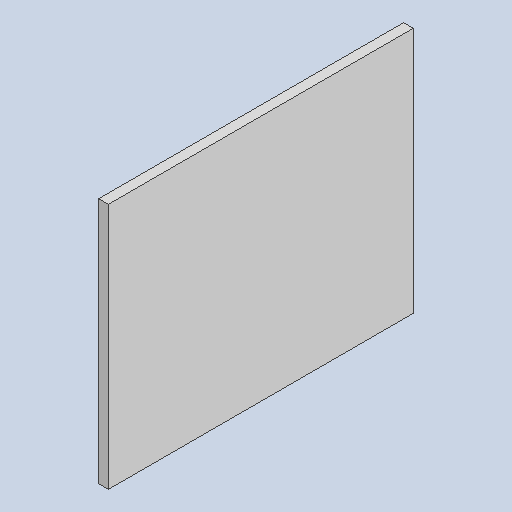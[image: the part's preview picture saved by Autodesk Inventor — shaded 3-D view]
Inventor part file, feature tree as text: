
AUTODESK INVENTOR PART (.ipt)
format: ipt  version: 2023 (Build 270158030, 158C)  size: 166,400 bytes
history: native  units: mm
features: extrude x4, sketch x4, other x3, reference x2
ambient origin geometry x8: Origin, YZ Plane, XZ Plane, XY Plane, X Axis, Y Axis, Z Axis, Center Point
bodies: Solid1 (feature_tree)
feature tree (13):
  extrude  "Extrusion1"  Depth=5.6mm
  extrude  "Extrusion2"  Depth=14.0mm
  extrude  "Extrusion3"  Depth=489.0mm
  extrude  "Extrusion4"  Depth=1.6mm TaperAngle=0.0deg
  sketch  "Sketch1"  dims[d1=5.6mm d2=5.0mm]
  reference  "Reference1"
  sketch  "Sketch2"  dims[d3=10.0mm d4=0.0mm d5=14.0mm]
  reference  "Reference2"
  sketch  "Sketch3"  dims[d6=489.0mm d7=3.0mm]
  sketch  "Sketch4"  dims[d8=3.0mm d9=1.6mm d10=0.0mm d11=396.0mm d12=1.6mm d13=0.0mm d14=1.6mm d15=1.6mm d16=1.6mm d17=1.6mm d18=0.0mm]
  other  "<userpath>\Documents\0004-inventor\Inventor_Projects\electronics-enclosure\enclosure.iam"
  other  "enclosure.iam"
  other  "enclosure-box:1"
